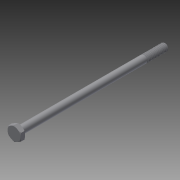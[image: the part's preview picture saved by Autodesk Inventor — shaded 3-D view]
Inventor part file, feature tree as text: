
AUTODESK INVENTOR PART (.ipt)
format: ipt  version: 2013 (Build 170138000, 138)  size: 340,992 bytes
history: native  units: in
note: dims shown in document units (in); Inventor stores cm internally (conversion verified against a paired STEP export)
features: extrude x1, other x1, imported_body x1
ambient origin geometry x8: Origin, YZ Plane, XZ Plane, XY Plane, X Axis, Y Axis, Z Axis, Center Point
feature tree (3):
  extrude  "Extrude14"  [1 undecoded]
  other  "91257A5601"
  imported_body  "Base1"
note: 1 required parameter value undecoded (feature->parameter linkage not recoverable at this tier; creation-order binding heuristic only, values carry confidence <= 0.55)
